FCSTD DOCUMENT  (FreeCAD 0.21R33771 (Git))
Label: sotexs
License: All rights reserved
LicenseURL: https://en.wikipedia.org/wiki/All_rights_reserved
objects: Part::Sphere×8, Part::Box×1, Part::Feature×1
note: 10 computed .brp shape members not serialized (recipe doc carries the construction recipe); baked Part::Feature solids carry a one-line shape summary decoded from their .brp

FEATURE [Part::Box] SourceBox
  AttacherType = Attacher::AttachEngine3D
  Height = 1000
  Length = 1000
  Placement = pos=(-500,-500,0) rot=(0,0,1;0rad)
  Width = 1000
FEATURE [Part::Sphere] M1
  Angle1 = -90
  Angle2 = 90
  Angle3 = 360
  AttacherType = Attacher::AttachEngine3D
  Placement = pos=(0,0,12000) rot=(0,0,1;0rad)
  Radius = 100
FEATURE [Part::Sphere] PremirrorM2
  Angle1 = -90
  Angle2 = 90
  Angle3 = 360
  AttacherType = Attacher::AttachEngine3D
  Placement = pos=(-145.892,3.17269,17969.5) rot=(0,0,1;0rad)
  Radius = 100
FEATURE [Part::Sphere] PG
  Angle1 = -90
  Angle2 = 90
  Angle3 = 360
  AttacherType = Attacher::AttachEngine3D
  Placement = pos=(-153.923,30,18298.1) rot=(0,0,1;0rad)
  Radius = 100
FEATURE [Part::Sphere] M3
  Angle1 = -90
  Angle2 = 90
  Angle3 = 360
  AttacherType = Attacher::AttachEngine3D
  Placement = pos=(-202.787,30,20297.5) rot=(0,0,1;0rad)
  Radius = 100
FEATURE [Part::Sphere] ExitSlit
  Angle1 = -90
  Angle2 = 90
  Angle3 = 360
  AttacherType = Attacher::AttachEngine3D
  Placement = pos=(-202.787,30,29797.5) rot=(0,0,1;0rad)
  Radius = 100
FEATURE [Part::Sphere] KB_ver
  Angle1 = -90
  Angle2 = 90
  Angle3 = 360
  AttacherType = Attacher::AttachEngine3D
  Placement = pos=(-202.787,30,33597.5) rot=(0,0,1;0rad)
  Radius = 100
FEATURE [Part::Sphere] KB_hor
  Angle1 = -90
  Angle2 = 90
  Angle3 = 360
  AttacherType = Attacher::AttachEngine3D
  Placement = pos=(-202.787,22.6703,33897.4) rot=(0,0,1;0rad)
  Radius = 100
FEATURE [Part::Sphere] DetectorAtFocus
  Angle1 = -90
  Angle2 = 90
  Angle3 = 360
  AttacherType = Attacher::AttachEngine3D
  Placement = pos=(-227.219,-1.75454,34896.8) rot=(0,0,1;0rad)
  Radius = 100
FEATURE [Part::Feature] BeamlinePath
  shape: bbox 227.2 x 31.75 x 34900 mm, 0 faces, 0 solids (baked)
